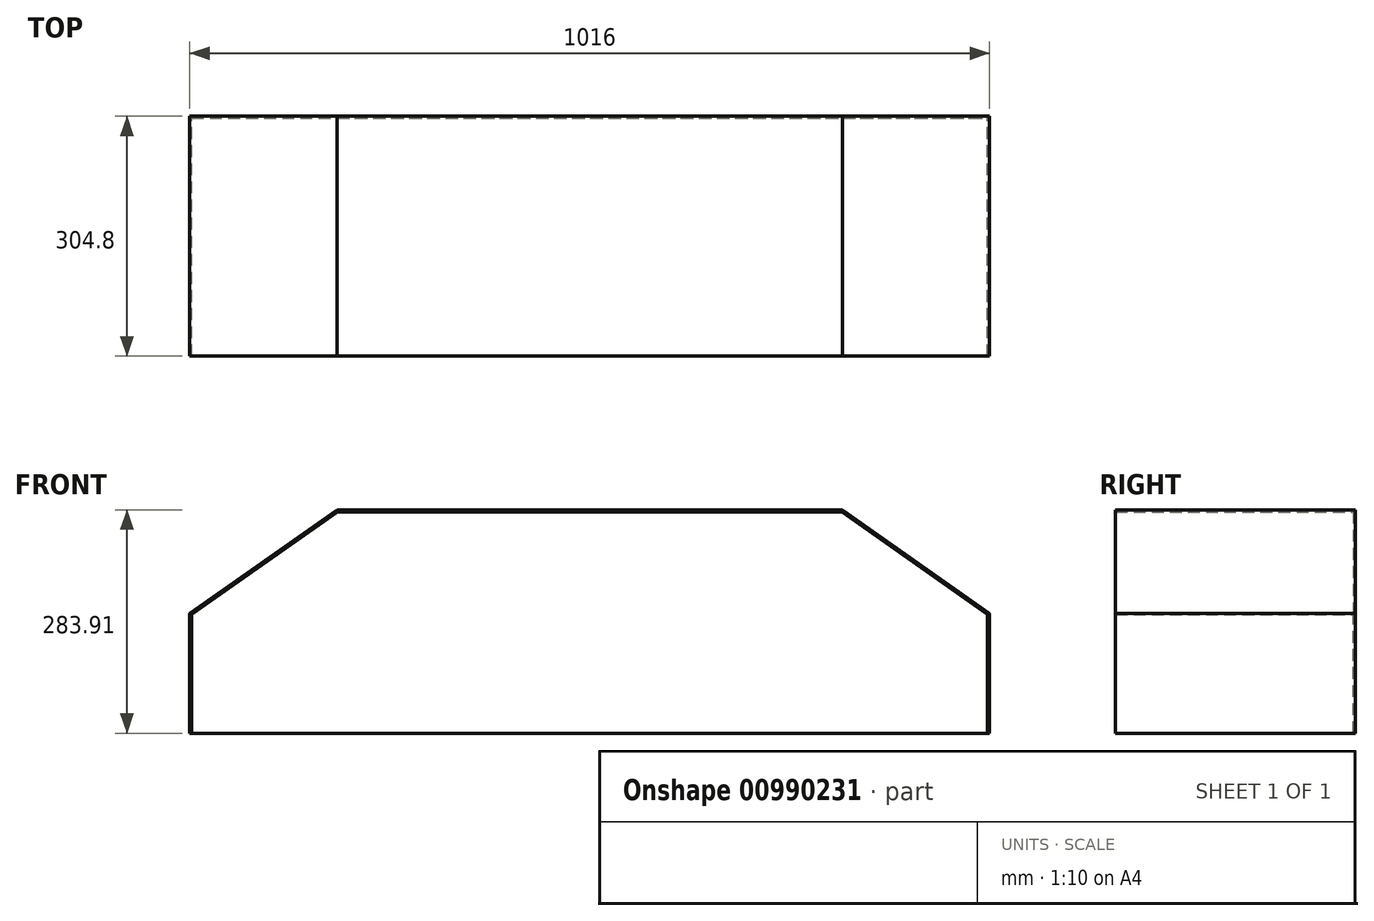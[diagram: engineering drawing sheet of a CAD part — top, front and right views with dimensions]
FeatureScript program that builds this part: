
annotation { "Feature Type Name" : "Feature", "Feature Type Description" : "" }
export const myFeature = defineFeature(function(context is Context, id is Id, definition is map)
    precondition{}
    {
        {
            var Q0;
            Q0=qCreatedBy(makeId("Front.planeOp"),FACE);
            var sketch = newSketch(context, id + "F0", { "sketchPlane" : qUnion([Q0])});
            skLineSegment(sketch, "E0", {"start": v(-508, 0) * mm, "end": v(508, 0) * mm});
            skLineSegment(sketch, "E1", {"start": v(-508, 0) * mm, "end": v(-508, 152.4) * mm});
            skLineSegment(sketch, "E2", {"start": v(508, 0) * mm, "end": v(508, 152.4) * mm});
            skLineSegment(sketch, "E3", {"start": v(-508, 152.4) * mm, "end": v(-321.01, 283.9) * mm});
            skLineSegment(sketch, "E4", {"start": v(-321.01, 283.9) * mm, "end": v(321.01, 283.9) * mm});
            skLineSegment(sketch, "E5", {"start": v(321.01, 283.9) * mm, "end": v(508, 152.4) * mm});
            skSolve(sketch);
        }
        {
            var Q0;
            Q0=makeQuery(id+"F0.imprint","IMPRINT",FACE,{"disambiguationData":[TD([[makeQuery(id+"F0.imprint","IMPRINT",EDGE,{"derivedFrom":sQuery(id+"F0.wireOp",EDGE,"E0")}),1.0]])]});
            extrude(context, id + "F1", {"entities" : qUnion([Q0]), "depth" : 304.8 * mm, "offsetDistance" : 25.4 * mm});
        }
        {
            var Q0;
            Q0=makeQuery(id+"F1.opExtrude","CAP_FACE",FACE,{"disambiguationData":[OSD([sQuery(id+"F0.wireOp",EDGE,"E0"),sQuery(id+"F0.wireOp",EDGE,"E1"),sQuery(id+"F0.wireOp",EDGE,"E2"),sQuery(id+"F0.wireOp",EDGE,"E3"),sQuery(id+"F0.wireOp",EDGE,"E4"),sQuery(id+"F0.wireOp",EDGE,"E5")])],"isStart":false});
            var Q1;
            Q1=makeQuery(id+"F1.opExtrude","SWEPT_FACE",FACE,{"disambiguationData":[OSD([sQuery(id+"F0.wireOp",EDGE,"E0")])]});
            shell(context, id + "F2", {"entities" : qUnion([Q0, Q1]), "thickness" : 2.54 * mm});
        }
    });
